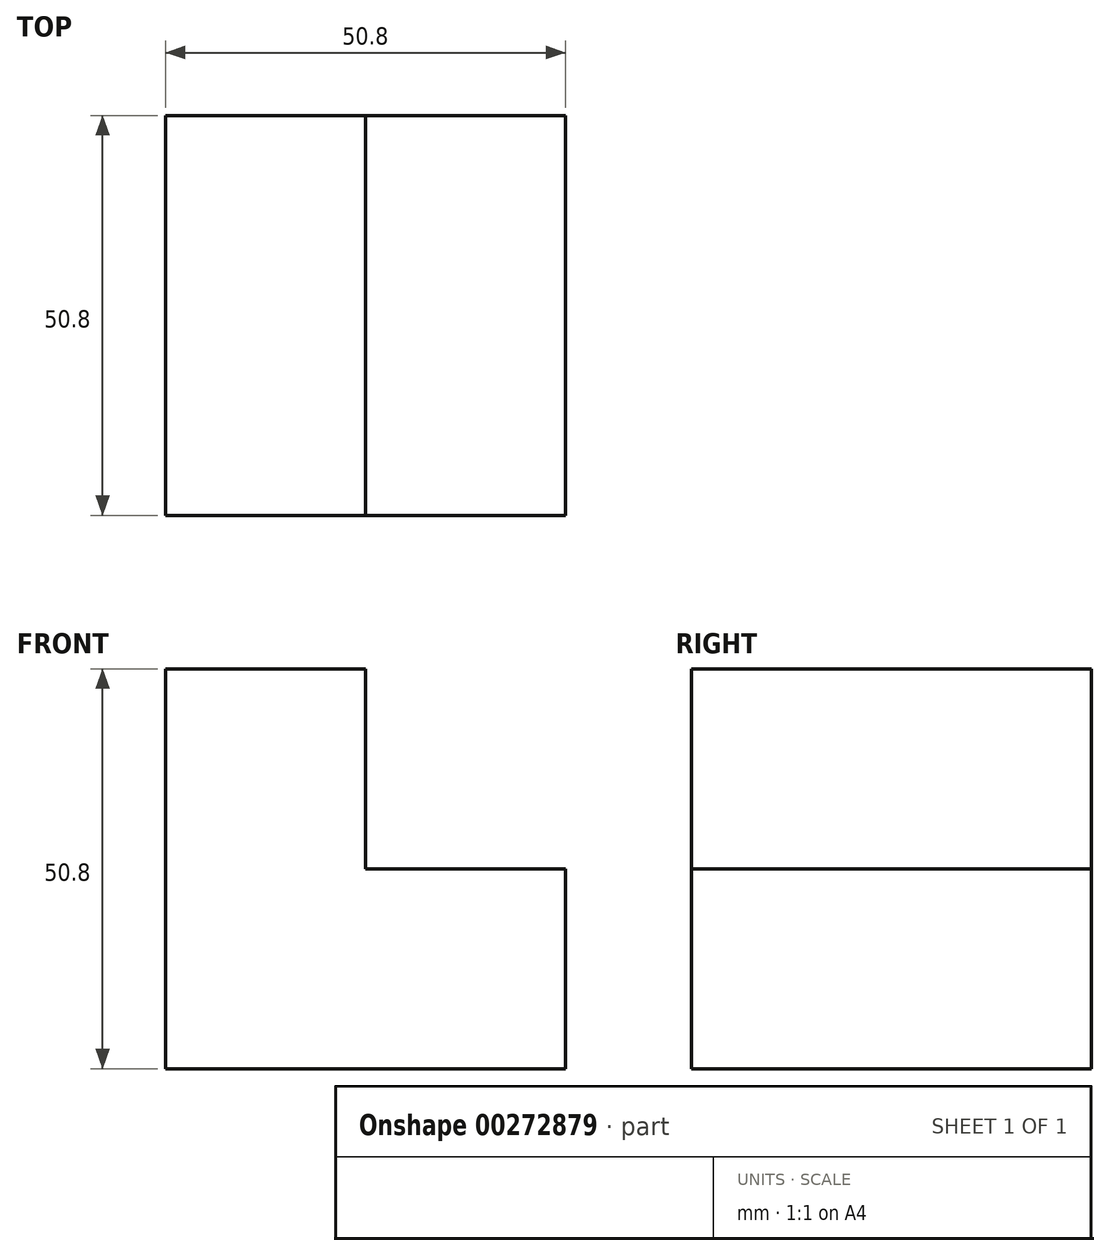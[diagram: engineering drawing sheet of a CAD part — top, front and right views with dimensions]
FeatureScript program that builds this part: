
annotation { "Feature Type Name" : "Feature", "Feature Type Description" : "" }
export const myFeature = defineFeature(function(context is Context, id is Id, definition is map)
    precondition{}
    {
        {
            var Q0;
            Q0=qCreatedBy(makeId("Front.planeOp"),FACE);
            var sketch = newSketch(context, id + "F0", { "sketchPlane" : qUnion([Q0])});
            skLineSegment(sketch, "E0", {"start": v(0, 0) * mm, "end": v(-50.8, 0) * mm});
            skLineSegment(sketch, "E1", {"start": v(-50.8, 0) * mm, "end": v(-50.8, 25.4) * mm});
            skLineSegment(sketch, "E2", {"start": v(-50.8, 25.4) * mm, "end": v(-50.8, 50.8) * mm});
            skLineSegment(sketch, "E3", {"start": v(-50.8, 50.8) * mm, "end": v(-25.4, 50.8) * mm});
            skLineSegment(sketch, "E4", {"start": v(-25.4, 50.8) * mm, "end": v(-25.4, 25.4) * mm});
            skLineSegment(sketch, "E5", {"start": v(-25.4, 25.4) * mm, "end": v(0, 25.4) * mm});
            skLineSegment(sketch, "E6", {"start": v(0, 25.4) * mm, "end": v(0, -4.4) * mm});
            skSolve(sketch);
        }
        {
            var Q0;
            Q0 = qSketchRegion(id + "F0", true);
            extrude(context, id + "F1", {"entities" : qUnion([Q0]), "depth" : 50.8 * mm});
        }
    });
